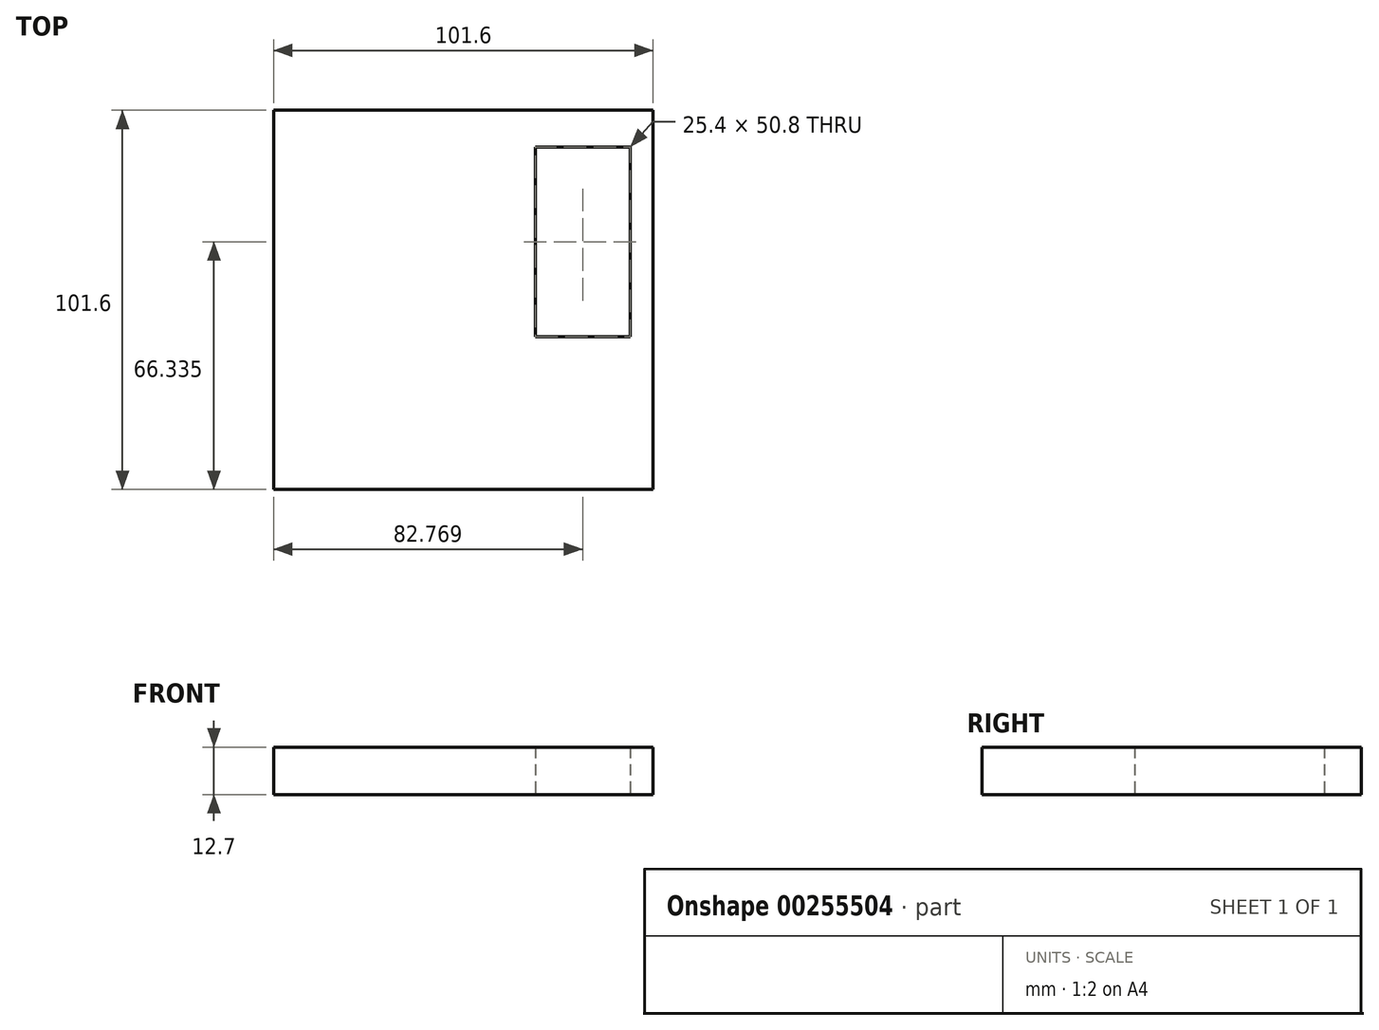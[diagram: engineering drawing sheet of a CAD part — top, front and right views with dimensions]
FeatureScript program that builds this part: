
annotation { "Feature Type Name" : "Feature", "Feature Type Description" : "" }
export const myFeature = defineFeature(function(context is Context, id is Id, definition is map)
    precondition{}
    {
        {
            var Q0;
            Q0=qCreatedBy(makeId("Top.planeOp"),FACE);
            var sketch = newSketch(context, id + "F0", { "sketchPlane" : qUnion([Q0])});
            skLineSegment(sketch, "E0.bottom", {"start": v(0, 0) * mm, "end": v(-101.6, 0) * mm});
            skLineSegment(sketch, "E0.top", {"start": v(0, 101.6) * mm, "end": v(-101.6, 101.6) * mm});
            skLineSegment(sketch, "E0.left", {"start": v(0, 0) * mm, "end": v(0, 101.6) * mm});
            skLineSegment(sketch, "E0.right", {"start": v(-101.6, 0) * mm, "end": v(-101.6, 101.6) * mm});
            skSolve(sketch);
        }
        {
            var Q0;
            Q0=makeQuery(id+"F0.imprint","IMPRINT",FACE,{"disambiguationData":[TD([[makeQuery(id+"F0.imprint","IMPRINT",EDGE,{"derivedFrom":sQuery(id+"F0.wireOp",EDGE,"E0.bottom")}),-1.0]])]});
            extrude(context, id + "F1", {"entities" : qUnion([Q0]), "depth" : 12.7 * mm});
        }
        {
            var Q0;
            Q0=makeQuery(id+"F1.opExtrude","CAP_FACE",FACE,{"disambiguationData":[OSD([sQuery(id+"F0.wireOp",EDGE,"E0.bottom"),sQuery(id+"F0.wireOp",EDGE,"E0.top"),sQuery(id+"F0.wireOp",EDGE,"E0.left"),sQuery(id+"F0.wireOp",EDGE,"E0.right")])],"isStart":true});
            var sketch = newSketch(context, id + "F2", { "sketchPlane" : qUnion([Q0])});
            skLineSegment(sketch, "E1", {"start": v(-101.6, -50.8) * mm, "end": v(-50.8, -50.8) * mm});
            skPoint(sketch, "E1.endSnap0", {"position": v(-50.8, 0) * mm});
            skLineSegment(sketch, "E2.bottom", {"start": v(-31.53, -91.74) * mm, "end": v(-6.13, -91.74) * mm});
            skLineSegment(sketch, "E2.top", {"start": v(-31.53, -40.94) * mm, "end": v(-6.13, -40.94) * mm});
            skLineSegment(sketch, "E2.left", {"start": v(-31.53, -91.74) * mm, "end": v(-31.53, -40.94) * mm});
            skLineSegment(sketch, "E2.right", {"start": v(-6.13, -91.74) * mm, "end": v(-6.13, -40.94) * mm});
            skSolve(sketch);
        }
        {
            var Q0;
            Q0=makeQuery(id+"F2.imprint","IMPRINT",FACE,{"disambiguationData":[TD([[makeQuery(id+"F2.imprint","IMPRINT",EDGE,{"derivedFrom":sQuery(id+"F2.wireOp",EDGE,"E2.bottom")}),1.0]])]});
            extrude(context, id + "F3", {"entities" : qUnion([Q0]), "operationType" : NewBodyOperationType.REMOVE, "oppositeDirection" : true, "depth" : 25.4 * mm});
        }
    });
